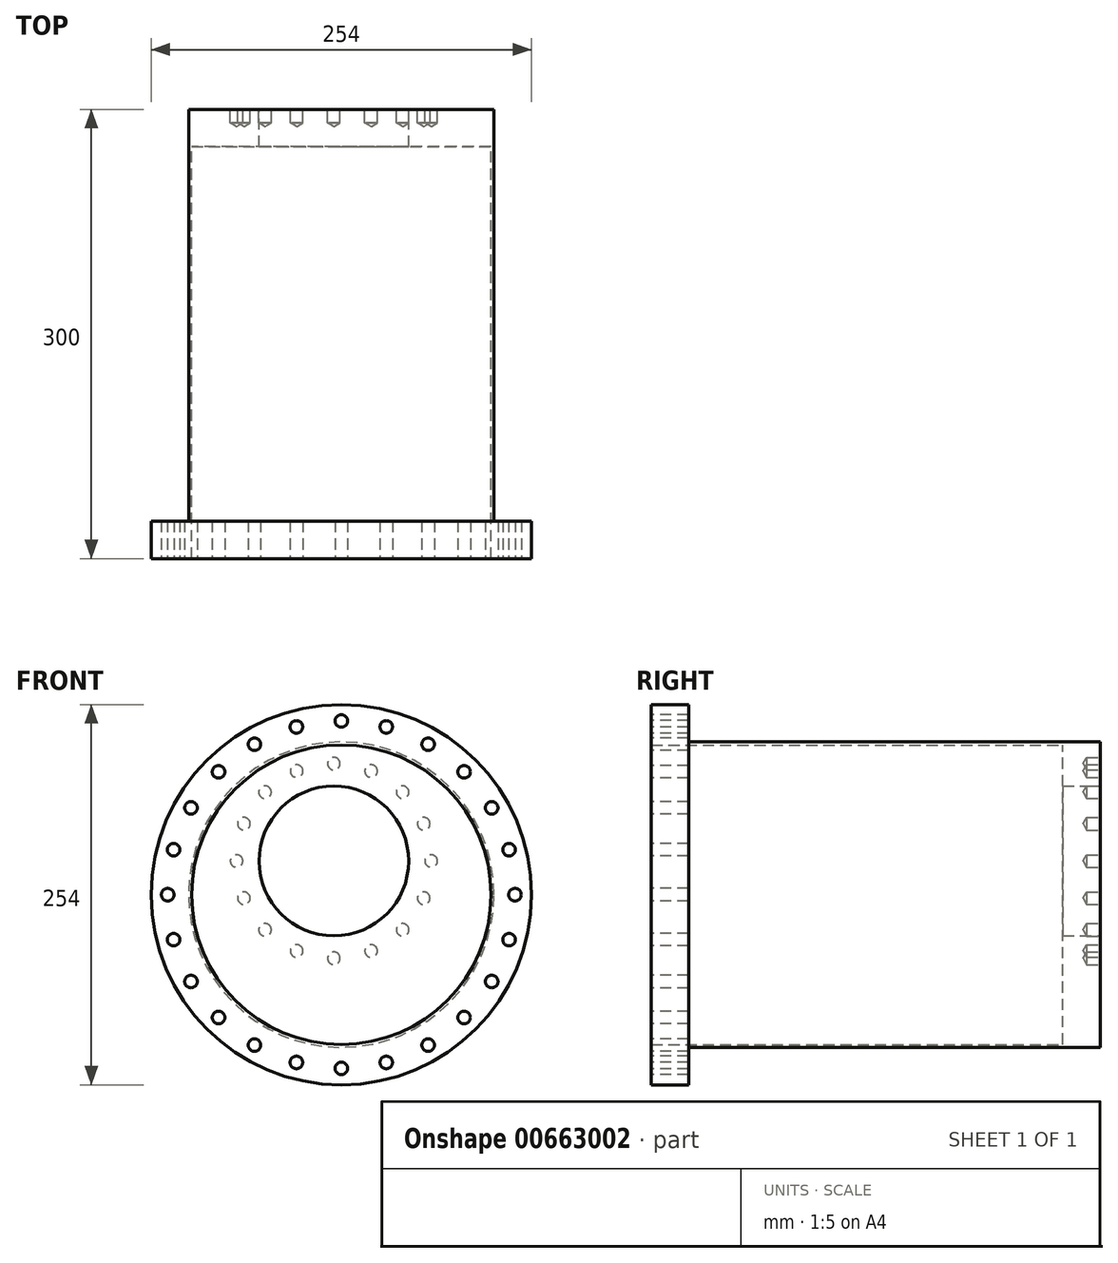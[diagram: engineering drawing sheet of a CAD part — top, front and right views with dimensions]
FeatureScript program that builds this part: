
annotation { "Feature Type Name" : "Feature", "Feature Type Description" : "" }
export const myFeature = defineFeature(function(context is Context, id is Id, definition is map)
    precondition{}
    {
        {
            var Q0;
            Q0=qCreatedBy(makeId("Front.planeOp"),FACE);
            var sketch = newSketch(context, id + "F0", { "sketchPlane" : qUnion([Q0])});
            skCircle(sketch, "E0", {"center": v(0, 0) * mm, "radius": 100 * mm});
            skCircle(sketch, "E1.0", {"center": v(0, 0) * mm, "radius": 102 * mm});
            skSolve(sketch);
        }
        {
            var Q0;
            Q0=makeQuery(id+"F0.imprint","IMPRINT",FACE,{"disambiguationData":[TD([[makeQuery(id+"F0.imprint","IMPRINT",EDGE,{"derivedFrom":sQuery(id+"F0.wireOp",EDGE,"E0")}),-1.0]])]});
            extrude(context, id + "F1", {"entities" : qUnion([Q0]), "depth" : (275 - 25) * mm, "offsetDistance" : 25 * mm});
        }
        {
            var Q0;
            Q0=makeQuery(id+"F1.opExtrude","CAP_FACE",FACE,{"disambiguationData":[OSD([sQuery(id+"F0.wireOp",EDGE,"E0"),sQuery(id+"F0.wireOp",EDGE,"E1.0")])],"isStart":false});
            var sketch = newSketch(context, id + "F2", { "sketchPlane" : qUnion([Q0])});
            skCircle(sketch, "E2", {"center": v(0, 0) * mm, "radius": 127 * mm});
            skSolve(sketch);
        }
        {
            var Q0;
            Q0=makeQuery(id+"F2.imprint","IMPRINT",FACE,{"disambiguationData":[TD([[makeQuery(id+"F2.imprint","IMPRINT",EDGE,{"derivedFrom":makeQuery(id+"F1.opExtrude","CAP_EDGE",EDGE,{"disambiguationData":[OSD([sQuery(id+"F0.wireOp",EDGE,"E0")])],"isStart":false})}),-1.0]])]});
            var Q1;
            Q1=makeQuery(id+"F2.imprint","IMPRINT",FACE,{"disambiguationData":[TD([[makeQuery(id+"F2.imprint","IMPRINT",EDGE,{"derivedFrom":sQuery(id+"F2.wireOp",EDGE,"E2")}),1.0]])]});
            extrude(context, id + "F3", {"entities" : qUnion([Q0, Q1]), "operationType" : NewBodyOperationType.ADD, "depth" : 25 * mm, "offsetDistance" : 25 * mm});
        }
        {
            var Q0;
            Q0=makeQuery(id+"F1.opExtrude","CAP_FACE",FACE,{"disambiguationData":[OSD([sQuery(id+"F0.wireOp",EDGE,"E0"),sQuery(id+"F0.wireOp",EDGE,"E1.0")])],"isStart":true});
            var sketch = newSketch(context, id + "F4", { "sketchPlane" : qUnion([Q0])});
            skCircle(sketch, "E3", {"center": v(0, 0) * mm, "radius": 102 * mm});
            skSolve(sketch);
        }
        {
            var Q0;
            Q0=makeQuery(id+"F4.imprint","IMPRINT",FACE,{"disambiguationData":[TD([[makeQuery(id+"F4.imprint","IMPRINT",EDGE,{"derivedFrom":makeQuery(id+"F1.opExtrude","CAP_EDGE",EDGE,{"disambiguationData":[OSD([sQuery(id+"F0.wireOp",EDGE,"E0")])],"isStart":true})}),-1.0]])]});
            var Q1;
            Q1=makeQuery(id+"F4.imprint","IMPRINT",FACE,{"disambiguationData":[TD([[makeQuery(id+"F4.imprint","IMPRINT",EDGE,{"derivedFrom":sQuery(id+"F4.wireOp",EDGE,"E3")}),-1.0]])]});
            extrude(context, id + "F5", {"entities" : qUnion([Q0, Q1]), "operationType" : NewBodyOperationType.ADD, "depth" : 25 * mm, "offsetDistance" : 25 * mm});
        }
        {
            var Q0;
            Q0=makeQuery(id+"F3.opExtrude","CAP_FACE",FACE,{"disambiguationData":[OSD([sQuery(id+"F0.wireOp",EDGE,"E0"),sQuery(id+"F2.wireOp",EDGE,"E2")])],"isStart":false});
            var sketch = newSketch(context, id + "F6", { "sketchPlane" : qUnion([Q0])});
            skCircle(sketch, "E4", {"center": v(0, 0) * mm, "radius": 116 * mm, "construction": true});
            skPoint(sketch, "E5", {"position": v(0, 116) * mm});
            skLineSegment(sketch, "E6", {"start": v(0, 0) * mm, "end": v(0, 116) * mm, "construction": true});
            skPoint(sketch, "E7.1.0", {"position": v(-30.02, 112.05) * mm});
            skPoint(sketch, "E7.2.0", {"position": v(-58, 100.46) * mm});
            skPoint(sketch, "E7.3.0", {"position": v(-82.02, 82.02) * mm});
            skPoint(sketch, "E7.4.0", {"position": v(-100.46, 58) * mm});
            skPoint(sketch, "E7.5.0", {"position": v(-112.05, 30.02) * mm});
            skPoint(sketch, "E7.6.0", {"position": v(-116, 0) * mm});
            skPoint(sketch, "E7.7.0", {"position": v(-112.05, -30.02) * mm});
            skPoint(sketch, "E7.8.0", {"position": v(-100.46, -58) * mm});
            skPoint(sketch, "E7.9.0", {"position": v(-82.02, -82.02) * mm});
            skPoint(sketch, "E7.10.0", {"position": v(-58, -100.46) * mm});
            skPoint(sketch, "E7.11.0", {"position": v(-30.02, -112.05) * mm});
            skPoint(sketch, "E7.12.0", {"position": v(0, -116) * mm});
            skPoint(sketch, "E7.13.0", {"position": v(30.02, -112.05) * mm});
            skPoint(sketch, "E7.14.0", {"position": v(58, -100.46) * mm});
            skPoint(sketch, "E7.15.0", {"position": v(82.02, -82.02) * mm});
            skPoint(sketch, "E7.16.0", {"position": v(100.46, -58) * mm});
            skPoint(sketch, "E7.17.0", {"position": v(112.05, -30.02) * mm});
            skPoint(sketch, "E7.18.0", {"position": v(116, 0) * mm});
            skPoint(sketch, "E7.19.0", {"position": v(112.05, 30.02) * mm});
            skPoint(sketch, "E7.20.0", {"position": v(100.46, 58) * mm});
            skPoint(sketch, "E7.21.0", {"position": v(82.02, 82.02) * mm});
            skPoint(sketch, "E7.22.0", {"position": v(58, 100.46) * mm});
            skPoint(sketch, "E7.23.0", {"position": v(30.02, 112.05) * mm});
            skSolve(sketch);
        }
        {
            var Q0;
            Q0=sQuery(id+"F6.wireOp",VERTEX,"E5");
            var Q1;
            Q1=sQuery(id+"F6.wireOp",VERTEX,"E7.23.0");
            var Q2;
            Q2=sQuery(id+"F6.wireOp",VERTEX,"E7.22.0");
            var Q3;
            Q3=sQuery(id+"F6.wireOp",VERTEX,"E7.21.0");
            var Q4;
            Q4=sQuery(id+"F6.wireOp",VERTEX,"E7.20.0");
            var Q5;
            Q5=sQuery(id+"F6.wireOp",VERTEX,"E7.19.0");
            var Q6;
            Q6=sQuery(id+"F6.wireOp",VERTEX,"E7.18.0");
            var Q7;
            Q7=sQuery(id+"F6.wireOp",VERTEX,"E7.17.0");
            var Q8;
            Q8=sQuery(id+"F6.wireOp",VERTEX,"E7.16.0");
            var Q9;
            Q9=sQuery(id+"F6.wireOp",VERTEX,"E7.15.0");
            var Q10;
            Q10=sQuery(id+"F6.wireOp",VERTEX,"E7.14.0");
            var Q11;
            Q11=sQuery(id+"F6.wireOp",VERTEX,"E7.13.0");
            var Q12;
            Q12=sQuery(id+"F6.wireOp",VERTEX,"E7.12.0");
            var Q13;
            Q13=sQuery(id+"F6.wireOp",VERTEX,"E7.11.0");
            var Q14;
            Q14=sQuery(id+"F6.wireOp",VERTEX,"E7.10.0");
            var Q15;
            Q15=sQuery(id+"F6.wireOp",VERTEX,"E7.9.0");
            var Q16;
            Q16=sQuery(id+"F6.wireOp",VERTEX,"E7.8.0");
            var Q17;
            Q17=sQuery(id+"F6.wireOp",VERTEX,"E7.7.0");
            var Q18;
            Q18=sQuery(id+"F6.wireOp",VERTEX,"E7.6.0");
            var Q19;
            Q19=sQuery(id+"F6.wireOp",VERTEX,"E7.5.0");
            var Q20;
            Q20=sQuery(id+"F6.wireOp",VERTEX,"E7.4.0");
            var Q21;
            Q21=sQuery(id+"F6.wireOp",VERTEX,"E7.3.0");
            var Q22;
            Q22=sQuery(id+"F6.wireOp",VERTEX,"E7.2.0");
            var Q23;
            Q23=sQuery(id+"F6.wireOp",VERTEX,"E7.1.0");
            var Q24;
            Q24=makeQuery(id+"F1.opExtrude","SWEPT_BODY",BODY,{"disambiguationData":[OSD([sQuery(id+"F0.wireOp",EDGE,"E0"),sQuery(id+"F0.wireOp",EDGE,"E1.0")])]});
            hole(context, id + "F7", {"style" : HoleStyle.SIMPLE, "endStyle" : HoleEndStyle.THROUGH, "standardTappedOrClearance" : lookupTablePath({ "fit" : "Close", "standard" : "ISO", "size" : "M8", "type" : "Clearance" }), "standardBlindInLast" : lookupTablePath({ "fit" : "Close", "standard" : "ISO", "engagement" : "75%", "pitch" : "1.25 mm", "size" : "M8", "type" : "Clearance & tapped" }), "holeDiameter" : 8.4 * mm, "majorDiameter" : 5 * mm, "isTappedThrough" : true, "tappedDepth" : 12 * mm, "tapClearance" : 3, "locations" : qUnion([Q0, Q1, Q2, Q3, Q4, Q5, Q6, Q7, Q8, Q9, Q10, Q11, Q12, Q13, Q14, Q15, Q16, Q17, Q18, Q19, Q20, Q21, Q22, Q23]), "scope" : qUnion([Q24])});
        }
        {
            var Q0;
            Q0=makeQuery(id+"F5.opExtrude","CAP_FACE",FACE,{"disambiguationData":[OSD([sQuery(id+"F4.wireOp",EDGE,"E3")])],"isStart":false});
            var sketch = newSketch(context, id + "F8", { "sketchPlane" : qUnion([Q0])});
            skCircle(sketch, "E8", {"center": v(5, 22.5) * mm, "radius": 50 * mm});
            skLineSegment(sketch, "E9", {"start": v(0, 0) * mm, "end": v(5, 22.5) * mm, "construction": true});
            skCircle(sketch, "E10", {"center": v(5, 22.5) * mm, "radius": 65 * mm, "construction": true});
            skPoint(sketch, "E11", {"position": v(5, 87.5) * mm});
            skPoint(sketch, "E12.1.0", {"position": v(-19.87, 82.55) * mm});
            skPoint(sketch, "E12.2.0", {"position": v(-40.96, 68.46) * mm});
            skPoint(sketch, "E12.3.0", {"position": v(-55.05, 47.37) * mm});
            skPoint(sketch, "E12.4.0", {"position": v(-60, 22.5) * mm});
            skPoint(sketch, "E12.5.0", {"position": v(-55.05, -2.37) * mm});
            skPoint(sketch, "E12.6.0", {"position": v(-40.96, -23.46) * mm});
            skPoint(sketch, "E12.7.0", {"position": v(-19.87, -37.55) * mm});
            skCircle(sketch, "E13", {"center": v(5, 22.5) * mm, "radius": 76 * mm, "construction": true});
            skPoint(sketch, "E14.0.8.0", {"position": v(5, -42.5) * mm});
            skPoint(sketch, "E14.0.9.0", {"position": v(29.87, -37.55) * mm});
            skPoint(sketch, "E14.0.10.0", {"position": v(50.96, -23.46) * mm});
            skPoint(sketch, "E14.0.11.0", {"position": v(65.05, -2.37) * mm});
            skPoint(sketch, "E14.0.12.0", {"position": v(70, 22.5) * mm});
            skPoint(sketch, "E14.0.13.0", {"position": v(65.05, 47.37) * mm});
            skPoint(sketch, "E14.0.14.0", {"position": v(50.96, 68.46) * mm});
            skPoint(sketch, "E14.0.15.0", {"position": v(29.87, 82.55) * mm});
            skSolve(sketch);
        }
        {
            var Q0;
            Q0=makeQuery(id+"F8.imprint","IMPRINT",FACE,{"disambiguationData":[TD([[makeQuery(id+"F8.imprint","IMPRINT",EDGE,{"derivedFrom":sQuery(id+"F8.wireOp",EDGE,"E8")}),1.0]])]});
            extrude(context, id + "F9", {"entities" : qUnion([Q0]), "operationType" : NewBodyOperationType.REMOVE, "endBound" : BoundingType.THROUGH_ALL, "oppositeDirection" : true, "depth" : 25 * mm, "offsetDistance" : 25 * mm});
        }
        {
            var Q0;
            Q0=sQuery(id+"F8.wireOp",VERTEX,"E11");
            var Q1;
            Q1=sQuery(id+"F8.wireOp",VERTEX,"E12.7.0");
            var Q2;
            Q2=sQuery(id+"F8.wireOp",VERTEX,"E12.6.0");
            var Q3;
            Q3=sQuery(id+"F8.wireOp",VERTEX,"E12.5.0");
            var Q4;
            Q4=sQuery(id+"F8.wireOp",VERTEX,"E12.4.0");
            var Q5;
            Q5=sQuery(id+"F8.wireOp",VERTEX,"E12.3.0");
            var Q6;
            Q6=sQuery(id+"F8.wireOp",VERTEX,"E12.2.0");
            var Q7;
            Q7=sQuery(id+"F8.wireOp",VERTEX,"E12.1.0");
            var Q8;
            Q8=sQuery(id+"F8.wireOp",VERTEX,"E14.0.15.0");
            var Q9;
            Q9=sQuery(id+"F8.wireOp",VERTEX,"E14.0.14.0");
            var Q10;
            Q10=sQuery(id+"F8.wireOp",VERTEX,"E14.0.13.0");
            var Q11;
            Q11=sQuery(id+"F8.wireOp",VERTEX,"E14.0.12.0");
            var Q12;
            Q12=sQuery(id+"F8.wireOp",VERTEX,"E14.0.11.0");
            var Q13;
            Q13=sQuery(id+"F8.wireOp",VERTEX,"E14.0.10.0");
            var Q14;
            Q14=sQuery(id+"F8.wireOp",VERTEX,"E14.0.9.0");
            var Q15;
            Q15=sQuery(id+"F8.wireOp",VERTEX,"E14.0.8.0");
            var Q16;
            Q16=makeQuery(id+"F1.opExtrude","SWEPT_BODY",BODY,{"disambiguationData":[OSD([sQuery(id+"F0.wireOp",EDGE,"E0"),sQuery(id+"F0.wireOp",EDGE,"E1.0")])]});
            hole(context, id + "F10", {"style" : HoleStyle.SIMPLE, "endStyle" : HoleEndStyle.BLIND, "standardTappedOrClearance" : lookupTablePath({ "fit" : "Close", "standard" : "ISO", "size" : "M8", "type" : "Clearance" }), "standardBlindInLast" : lookupTablePath({ "fit" : "Close", "standard" : "ISO", "engagement" : "75%", "pitch" : "1.25 mm", "size" : "M8", "type" : "Clearance & tapped" }), "holeDiameter" : 8.4 * mm, "majorDiameter" : 5 * mm, "holeDepth" : 9 * mm, "isTappedThrough" : true, "tappedDepth" : 12 * mm, "tapClearance" : 3, "locations" : qUnion([Q0, Q1, Q2, Q3, Q4, Q5, Q6, Q7, Q8, Q9, Q10, Q11, Q12, Q13, Q14, Q15]), "scope" : qUnion([Q16])});
        }
    });
